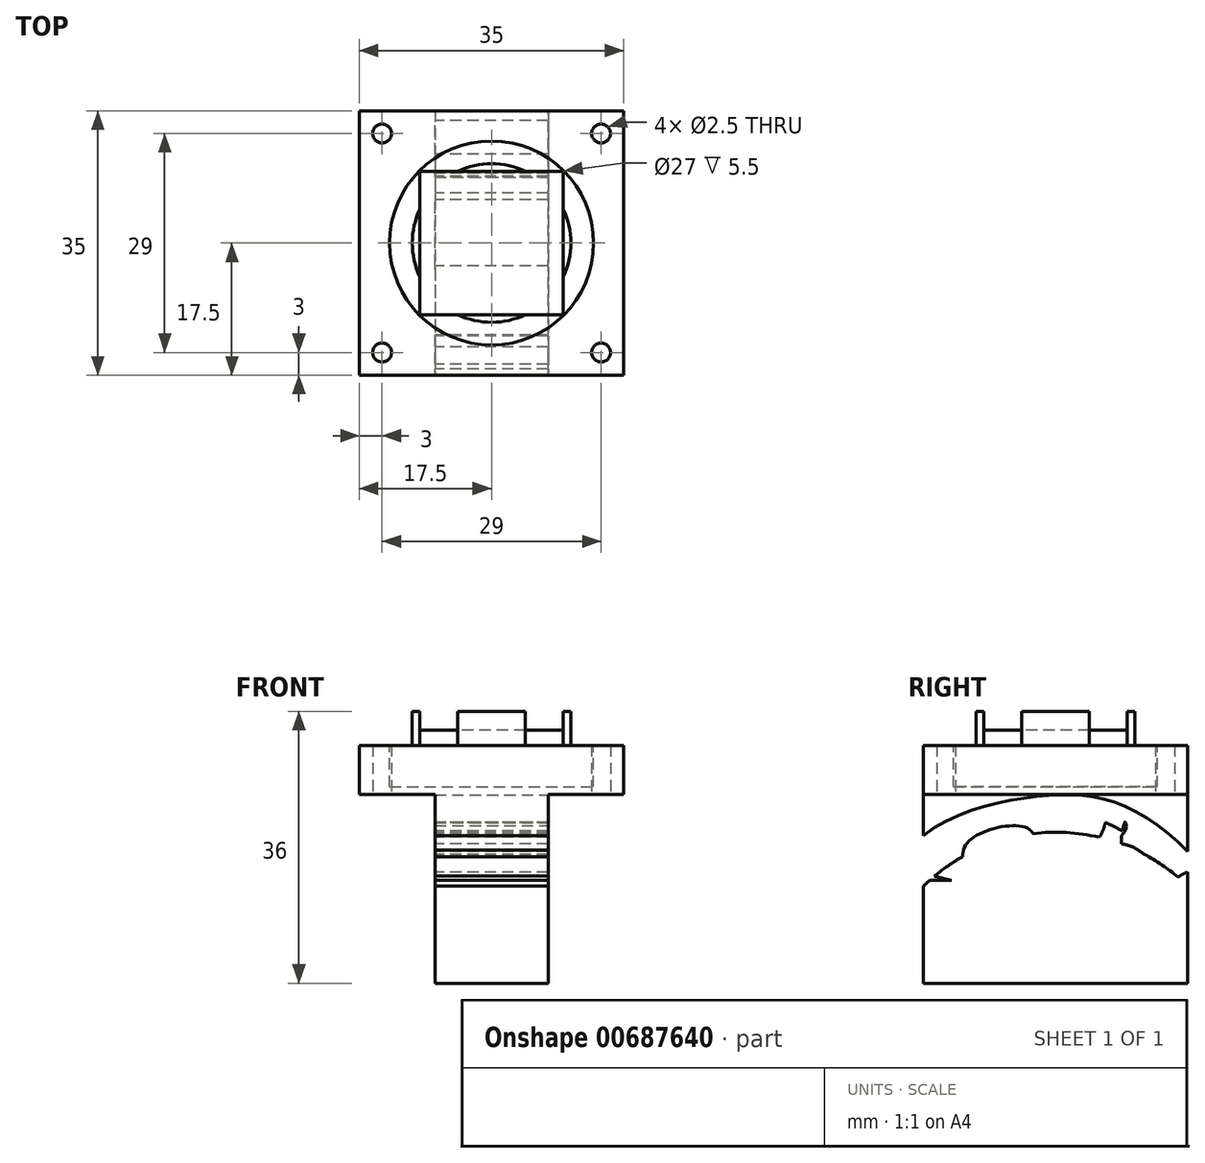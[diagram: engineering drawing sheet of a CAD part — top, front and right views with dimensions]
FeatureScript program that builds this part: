
annotation { "Feature Type Name" : "Feature", "Feature Type Description" : "" }
export const myFeature = defineFeature(function(context is Context, id is Id, definition is map)
    precondition{}
    {
        {
            var Q0;
            Q0=qCreatedBy(makeId("Top.planeOp"),FACE);
            var sketch = newSketch(context, id + "F0", { "sketchPlane" : qUnion([Q0])});
            skLineSegment(sketch, "E0", {"start": v(0, 0) * mm, "end": v(-19, 0) * mm});
            skLineSegment(sketch, "E1", {"start": v(-19, 0) * mm, "end": v(-19, 19) * mm});
            skLineSegment(sketch, "E2", {"start": v(-19, 19) * mm, "end": v(0, 19) * mm});
            skLineSegment(sketch, "E3", {"start": v(0, 19) * mm, "end": v(0, 0) * mm});
            skLineSegment(sketch, "E4.0", {"start": v(2, -2) * mm, "end": v(-21, -2) * mm});
            skLineSegment(sketch, "E4.1", {"start": v(2, 21) * mm, "end": v(2, -2) * mm});
            skLineSegment(sketch, "E4.2", {"start": v(-21, 21) * mm, "end": v(2, 21) * mm});
            skLineSegment(sketch, "E4.3", {"start": v(-21, -2) * mm, "end": v(-21, 21) * mm});
            skCircle(sketch, "E5", {"center": v(-9.5, 9.5) * mm, "radius": 10.5 * mm});
            skPoint(sketch, "E5.centerSnap0", {"position": v(-9.5, 0) * mm});
            skPoint(sketch, "E5.centerSnap1", {"position": v(0, 9.5) * mm});
            skLineSegment(sketch, "E6.0", {"start": v(8, -8) * mm, "end": v(-27, -8) * mm});
            skLineSegment(sketch, "E6.1", {"start": v(8, 27) * mm, "end": v(8, -8) * mm});
            skLineSegment(sketch, "E6.2", {"start": v(-27, 27) * mm, "end": v(8, 27) * mm});
            skLineSegment(sketch, "E6.3", {"start": v(-27, -8) * mm, "end": v(-27, 27) * mm});
            skLineSegment(sketch, "E7", {"start": v(-27, -8) * mm, "end": v(-21, -2) * mm});
            skLineSegment(sketch, "E8", {"start": v(-27, -8) * mm, "end": v(-24, -5) * mm});
            skLineSegment(sketch, "E9", {"start": v(-9.5, 9.5) * mm, "end": v(-11.5, 9.5) * mm});
            skLineSegment(sketch, "E10", {"start": v(-9.5, 9.5) * mm, "end": v(-9.5, 11.53) * mm});
            skLineSegment(sketch, "E11.MirrorCS", {"start": v(-27, 27) * mm, "end": v(-24, 24) * mm});
            skLineSegment(sketch, "E12.MirrorCS", {"start": v(8, -8) * mm, "end": v(5, -5) * mm});
            skLineSegment(sketch, "E13.MirrorCS", {"start": v(8, 27) * mm, "end": v(5, 24) * mm});
            skSolve(sketch);
        }
        {
            var Q0;
            Q0=qSketchRegion(id+"F0",true);
            var Q1;
            {var subQ0=sQuery(id+"F0.wireOp",EDGE,"E5");var subQ1=sQuery(id+"F0.wireOp",EDGE,"E3");var subQ2=makeQuery(id+"F0.imprint","INTERSECT",VERTEX,{"disambiguationData":[OD(0.0)],"derivedFrom":[subQ1,subQ0]});Q1=makeQuery(id+"F0.imprint","IMPRINT",FACE,{"disambiguationData":[TD([[makeQuery(id+"F0.imprint","IMPRINT",EDGE,{"disambiguationData":[TD([[subQ2,-1.0]])],"derivedFrom":subQ1}),1.0]])]});}
            var Q2;
            {var subQ0=sQuery(id+"F0.wireOp",EDGE,"E5");var subQ1=sQuery(id+"F0.wireOp",EDGE,"E0");var subQ2=makeQuery(id+"F0.imprint","INTERSECT",VERTEX,{"disambiguationData":[OD(0.0)],"derivedFrom":[subQ1,subQ0]});Q2=makeQuery(id+"F0.imprint","IMPRINT",FACE,{"disambiguationData":[TD([[makeQuery(id+"F0.imprint","IMPRINT",EDGE,{"disambiguationData":[TD([[subQ2,-1.0]])],"derivedFrom":subQ1}),1.0]])]});}
            var Q3;
            {var subQ0=sQuery(id+"F0.wireOp",EDGE,"E5");var subQ1=sQuery(id+"F0.wireOp",EDGE,"E1");var subQ2=makeQuery(id+"F0.imprint","INTERSECT",VERTEX,{"disambiguationData":[OD(0.0)],"derivedFrom":[subQ1,subQ0]});Q3=makeQuery(id+"F0.imprint","IMPRINT",FACE,{"disambiguationData":[TD([[makeQuery(id+"F0.imprint","IMPRINT",EDGE,{"disambiguationData":[TD([[subQ2,-1.0]])],"derivedFrom":subQ1}),1.0]])]});}
            var Q4;
            {var subQ0=sQuery(id+"F0.wireOp",EDGE,"E5");var subQ1=sQuery(id+"F0.wireOp",EDGE,"E2");var subQ2=makeQuery(id+"F0.imprint","INTERSECT",VERTEX,{"disambiguationData":[OD(0.0)],"derivedFrom":[subQ1,subQ0]});Q4=makeQuery(id+"F0.imprint","IMPRINT",FACE,{"disambiguationData":[TD([[makeQuery(id+"F0.imprint","IMPRINT",EDGE,{"disambiguationData":[TD([[subQ2,-1.0]])],"derivedFrom":subQ1}),1.0]])]});}
            var Q5;
            {var subQ0=sQuery(id+"F0.wireOp",EDGE,"E2");var subQ1=sQuery(id+"F0.wireOp",EDGE,"E1");var subQ2=makeQuery(id+"F0.imprint","INTERSECT",VERTEX,{"derivedFrom":[subQ1,subQ0]});Q5=makeQuery(id+"F0.imprint","IMPRINT",FACE,{"disambiguationData":[TD([[makeQuery(id+"F0.imprint","IMPRINT",EDGE,{"disambiguationData":[TD([[subQ2,1.0]])],"derivedFrom":subQ1}),-1.0]])]});}
            var Q6;
            {var subQ0=sQuery(id+"F0.wireOp",EDGE,"E3");var subQ1=sQuery(id+"F0.wireOp",EDGE,"E2");var subQ2=makeQuery(id+"F0.imprint","INTERSECT",VERTEX,{"derivedFrom":[subQ1,subQ0]});Q6=makeQuery(id+"F0.imprint","IMPRINT",FACE,{"disambiguationData":[TD([[makeQuery(id+"F0.imprint","IMPRINT",EDGE,{"disambiguationData":[TD([[subQ2,1.0]])],"derivedFrom":subQ1}),-1.0]])]});}
            var Q7;
            {var subQ0=sQuery(id+"F0.wireOp",EDGE,"E3");var subQ1=sQuery(id+"F0.wireOp",EDGE,"E0");var subQ2=makeQuery(id+"F0.imprint","INTERSECT",VERTEX,{"derivedFrom":[subQ1,subQ0]});Q7=makeQuery(id+"F0.imprint","IMPRINT",FACE,{"disambiguationData":[TD([[makeQuery(id+"F0.imprint","IMPRINT",EDGE,{"disambiguationData":[TD([[subQ2,-1.0]])],"derivedFrom":subQ1}),-1.0]])]});}
            var Q8;
            {var subQ0=sQuery(id+"F0.wireOp",EDGE,"E1");var subQ1=sQuery(id+"F0.wireOp",EDGE,"E0");var subQ2=makeQuery(id+"F0.imprint","INTERSECT",VERTEX,{"derivedFrom":[subQ1,subQ0]});Q8=makeQuery(id+"F0.imprint","IMPRINT",FACE,{"disambiguationData":[TD([[makeQuery(id+"F0.imprint","IMPRINT",EDGE,{"disambiguationData":[TD([[subQ2,1.0]])],"derivedFrom":subQ1}),-1.0]])]});}
            var Q9;
            Q9=makeQuery(id+"F0.imprint","IMPRINT",FACE,{"disambiguationData":[TD([[makeQuery(id+"F0.imprint","IMPRINT",EDGE,{"derivedFrom":sQuery(id+"F0.wireOp",EDGE,"E4.0")}),-1.0]])]});
            var Q10;
            {var subQ0=sQuery(id+"F0.wireOp",EDGE,"E5");var subQ10=sQuery(id+"F0.wireOp",EDGE,"E0");var subQ11=makeQuery(id+"F0.imprint","INTERSECT",VERTEX,{"disambiguationData":[OD(0.0)],"derivedFrom":[subQ10,subQ0]});Q10=makeQuery(id+"F0.imprint","IMPRINT",FACE,{"disambiguationData":[TD([[makeQuery(id+"F0.imprint","IMPRINT",EDGE,{"disambiguationData":[TD([[subQ11,-1.0]])],"derivedFrom":subQ10}),-1.0]])]});}
            extrude(context, id + "F1", {"entities" : qUnion([Q0, Q1, Q2, Q3, Q4, Q5, Q6, Q7, Q8, Q9, Q10]), "oppositeDirection" : true, "depth" : 2 * mm, "offsetDistance" : 25 * mm});
        }
        {
            var Q0;
            Q0=makeQuery(id+"F1.opExtrude","CAP_FACE",FACE,{"disambiguationData":[OSD([sQuery(id+"F0.wireOp",EDGE,"E6.0"),sQuery(id+"F0.wireOp",EDGE,"E6.1"),sQuery(id+"F0.wireOp",EDGE,"E6.2"),sQuery(id+"F0.wireOp",EDGE,"E6.3")])],"isStart":false});
            var sketch = newSketch(context, id + "F2", { "sketchPlane" : qUnion([Q0])});
            skLineSegment(sketch, "E14", {"start": v(-27, -27) * mm, "end": v(-27, 8) * mm});
            skLineSegment(sketch, "E15", {"start": v(-27, 8) * mm, "end": v(8, 8) * mm});
            skLineSegment(sketch, "E16", {"start": v(8, 8) * mm, "end": v(8, -27) * mm});
            skLineSegment(sketch, "E17", {"start": v(8, -27) * mm, "end": v(-27, -27) * mm});
            skLineSegment(sketch, "E18", {"start": v(-27, -9.5) * mm, "end": v(8, -9.5) * mm});
            skCircle(sketch, "E19", {"center": v(-9.5, -9.5) * mm, "radius": 13.5 * mm});
            skSolve(sketch);
        }
        {
            var Q0;
            Q0=qSketchRegion(id+"F2",true);
            extrude(context, id + "F3", {"entities" : qUnion([Q0]), "depth" : 5.5 * mm, "offsetDistance" : 25 * mm});
        }
        {
            var Q0;
            {var subQ0=sQuery(id+"F0.wireOp",EDGE,"E5");var subQ1=sQuery(id+"F0.wireOp",EDGE,"E1");var subQ2=makeQuery(id+"F0.imprint","INTERSECT",VERTEX,{"disambiguationData":[OD(0.0)],"derivedFrom":[subQ1,subQ0]});Q0=makeQuery(id+"F0.imprint","IMPRINT",FACE,{"disambiguationData":[TD([[makeQuery(id+"F0.imprint","IMPRINT",EDGE,{"disambiguationData":[TD([[subQ2,-1.0]])],"derivedFrom":subQ1}),1.0]])]});}
            var Q1;
            {var subQ0=sQuery(id+"F0.wireOp",EDGE,"E5");var subQ1=sQuery(id+"F0.wireOp",EDGE,"E2");var subQ2=makeQuery(id+"F0.imprint","INTERSECT",VERTEX,{"disambiguationData":[OD(0.0)],"derivedFrom":[subQ1,subQ0]});Q1=makeQuery(id+"F0.imprint","IMPRINT",FACE,{"disambiguationData":[TD([[makeQuery(id+"F0.imprint","IMPRINT",EDGE,{"disambiguationData":[TD([[subQ2,-1.0]])],"derivedFrom":subQ1}),1.0]])]});}
            var Q2;
            {var subQ0=sQuery(id+"F0.wireOp",EDGE,"E5");var subQ1=sQuery(id+"F0.wireOp",EDGE,"E3");var subQ2=makeQuery(id+"F0.imprint","INTERSECT",VERTEX,{"disambiguationData":[OD(0.0)],"derivedFrom":[subQ1,subQ0]});Q2=makeQuery(id+"F0.imprint","IMPRINT",FACE,{"disambiguationData":[TD([[makeQuery(id+"F0.imprint","IMPRINT",EDGE,{"disambiguationData":[TD([[subQ2,-1.0]])],"derivedFrom":subQ1}),1.0]])]});}
            var Q3;
            {var subQ0=sQuery(id+"F0.wireOp",EDGE,"E5");var subQ1=sQuery(id+"F0.wireOp",EDGE,"E0");var subQ2=makeQuery(id+"F0.imprint","INTERSECT",VERTEX,{"disambiguationData":[OD(0.0)],"derivedFrom":[subQ1,subQ0]});Q3=makeQuery(id+"F0.imprint","IMPRINT",FACE,{"disambiguationData":[TD([[makeQuery(id+"F0.imprint","IMPRINT",EDGE,{"disambiguationData":[TD([[subQ2,-1.0]])],"derivedFrom":subQ1}),1.0]])]});}
            var Q4;
            Q4=makeQuery(id+"F0.imprint","IMPRINT",FACE,{"disambiguationData":[TD([[makeQuery(id+"F0.imprint","IMPRINT",EDGE,{"derivedFrom":sQuery(id+"F0.wireOp",EDGE,"E4.0")}),-1.0]])]});
            extrude(context, id + "F4", {"entities" : qUnion([Q0, Q1, Q2, Q3, Q4]), "operationType" : NewBodyOperationType.ADD, "depth" : 2.5 * mm, "offsetDistance" : 25 * mm});
        }
        {
            var Q0;
            Q0=makeQuery(id+"F3.opExtrude","CAP_FACE",FACE,{"disambiguationData":[OSD([sQuery(id+"F2.wireOp",EDGE,"E14"),sQuery(id+"F2.wireOp",EDGE,"E15"),sQuery(id+"F2.wireOp",EDGE,"E16"),sQuery(id+"F2.wireOp",EDGE,"E17"),sQuery(id+"F2.wireOp",EDGE,"E19")])],"isStart":false});
            var Q1;
            Q1=makeQuery(id+"F1.opExtrude","CAP_FACE",FACE,{"disambiguationData":[OSD([sQuery(id+"F0.wireOp",EDGE,"E6.0"),sQuery(id+"F0.wireOp",EDGE,"E6.1"),sQuery(id+"F0.wireOp",EDGE,"E6.2"),sQuery(id+"F0.wireOp",EDGE,"E6.3")])],"isStart":false});
            extrude(context, id + "F5", {"entities" : qUnion([Q0, Q1]), "depth" : 1 * mm, "offsetDistance" : 25 * mm});
        }
        {
            var Q0;
            Q0=makeQuery(id+"F5.opExtrude","SWEPT_BODY",BODY,{"disambiguationData":[OSD([sQuery(id+"F2.wireOp",EDGE,"E14"),sQuery(id+"F2.wireOp",EDGE,"E15"),sQuery(id+"F2.wireOp",EDGE,"E16"),sQuery(id+"F2.wireOp",EDGE,"E17"),sQuery(id+"F2.wireOp",EDGE,"E19")])]});
            var Q1;
            Q1=makeQuery(id+"F5.opExtrude","SWEPT_BODY",BODY,{"disambiguationData":[OSD([sQuery(id+"F0.wireOp",EDGE,"E6.0"),sQuery(id+"F0.wireOp",EDGE,"E6.1"),sQuery(id+"F0.wireOp",EDGE,"E6.2"),sQuery(id+"F0.wireOp",EDGE,"E6.3")])]});
            deleteBodies(context, id + "F6", {"entities" : qUnion([Q0, Q1])});
        }
        {
            var Q0;
            Q0=makeQuery(id+"F3.opExtrude","CAP_FACE",FACE,{"disambiguationData":[OSD([sQuery(id+"F2.wireOp",EDGE,"E14"),sQuery(id+"F2.wireOp",EDGE,"E15"),sQuery(id+"F2.wireOp",EDGE,"E16"),sQuery(id+"F2.wireOp",EDGE,"E17"),sQuery(id+"F2.wireOp",EDGE,"E19")])],"isStart":false});
            var sketch = newSketch(context, id + "F7", { "sketchPlane" : qUnion([Q0])});
            skLineSegment(sketch, "E20", {"start": v(-27, -27) * mm, "end": v(8, -27) * mm});
            skLineSegment(sketch, "E21", {"start": v(8, -27) * mm, "end": v(8, 8) * mm});
            skLineSegment(sketch, "E22", {"start": v(8, 8) * mm, "end": v(-27, 8) * mm});
            skLineSegment(sketch, "E23", {"start": v(-27, 8) * mm, "end": v(-27, -27) * mm});
            skSolve(sketch);
        }
        {
            var Q0;
            Q0=makeQuery(id+"F7.imprint","IMPRINT",FACE,{"disambiguationData":[TD([[makeQuery(id+"F7.imprint","IMPRINT",EDGE,{"derivedFrom":sQuery(id+"F7.wireOp",EDGE,"E20")}),1.0]])]});
            var Q1;
            Q1=makeQuery(id+"F7.imprint","IMPRINT",FACE,{"disambiguationData":[TD([[makeQuery(id+"F7.imprint","IMPRINT",EDGE,{"derivedFrom":makeQuery(id+"FP3SZp29wrBzVes_1.hole-0.boolean.opBoolean","INTERSECT",EDGE,{"derivedFrom":[makeQuery(id+"F3.opExtrude","CAP_FACE",FACE,{"disambiguationData":[OSD([sQuery(id+"F2.wireOp",EDGE,"E14"),sQuery(id+"F2.wireOp",EDGE,"E15"),sQuery(id+"F2.wireOp",EDGE,"E16"),sQuery(id+"F2.wireOp",EDGE,"E17"),sQuery(id+"F2.wireOp",EDGE,"E19")])],"isStart":false}),makeQuery(id+"FP3SZp29wrBzVes_1.hole-0.opRevolve","SWEPT_FACE",FACE,{"disambiguationData":[OSD([sQuery(id+"FP3SZp29wrBzVes_1.hole-0.sketch.wireOp",EDGE,"core_line_2")])]})]})}),-1.0]])]});
            var Q2;
            Q2=makeQuery(id+"F7.imprint","IMPRINT",FACE,{"disambiguationData":[TD([[makeQuery(id+"F7.imprint","IMPRINT",EDGE,{"derivedFrom":makeQuery(id+"FP3SZp29wrBzVes_1.hole-1.boolean.opBoolean","INTERSECT",EDGE,{"derivedFrom":[makeQuery(id+"F3.opExtrude","CAP_FACE",FACE,{"disambiguationData":[OSD([sQuery(id+"F2.wireOp",EDGE,"E14"),sQuery(id+"F2.wireOp",EDGE,"E15"),sQuery(id+"F2.wireOp",EDGE,"E16"),sQuery(id+"F2.wireOp",EDGE,"E17"),sQuery(id+"F2.wireOp",EDGE,"E19")])],"isStart":false}),makeQuery(id+"FP3SZp29wrBzVes_1.hole-1.opRevolve","SWEPT_FACE",FACE,{"disambiguationData":[OSD([sQuery(id+"FP3SZp29wrBzVes_1.hole-1.sketch.wireOp",EDGE,"core_line_2")])]})]})}),-1.0]])]});
            var Q3;
            Q3=makeQuery(id+"F7.imprint","IMPRINT",FACE,{"disambiguationData":[TD([[makeQuery(id+"F7.imprint","IMPRINT",EDGE,{"derivedFrom":makeQuery(id+"FP3SZp29wrBzVes_1.hole-3.boolean.opBoolean","INTERSECT",EDGE,{"derivedFrom":[makeQuery(id+"F3.opExtrude","CAP_FACE",FACE,{"disambiguationData":[OSD([sQuery(id+"F2.wireOp",EDGE,"E14"),sQuery(id+"F2.wireOp",EDGE,"E15"),sQuery(id+"F2.wireOp",EDGE,"E16"),sQuery(id+"F2.wireOp",EDGE,"E17"),sQuery(id+"F2.wireOp",EDGE,"E19")])],"isStart":false}),makeQuery(id+"FP3SZp29wrBzVes_1.hole-3.opRevolve","SWEPT_FACE",FACE,{"disambiguationData":[OSD([sQuery(id+"FP3SZp29wrBzVes_1.hole-3.sketch.wireOp",EDGE,"core_line_2")])]})]})}),-1.0]])]});
            var Q4;
            Q4=makeQuery(id+"F7.imprint","IMPRINT",FACE,{"disambiguationData":[TD([[makeQuery(id+"F7.imprint","IMPRINT",EDGE,{"derivedFrom":makeQuery(id+"F3.opExtrude","CAP_EDGE",EDGE,{"disambiguationData":[OSD([sQuery(id+"F2.wireOp",EDGE,"E19")])],"isStart":false})}),1.0]])]});
            var Q5;
            Q5=makeQuery(id+"F7.imprint","IMPRINT",FACE,{"disambiguationData":[TD([[makeQuery(id+"F7.imprint","IMPRINT",EDGE,{"derivedFrom":makeQuery(id+"FP3SZp29wrBzVes_1.hole-2.boolean.opBoolean","INTERSECT",EDGE,{"derivedFrom":[makeQuery(id+"F3.opExtrude","CAP_FACE",FACE,{"disambiguationData":[OSD([sQuery(id+"F2.wireOp",EDGE,"E14"),sQuery(id+"F2.wireOp",EDGE,"E15"),sQuery(id+"F2.wireOp",EDGE,"E16"),sQuery(id+"F2.wireOp",EDGE,"E17"),sQuery(id+"F2.wireOp",EDGE,"E19")])],"isStart":false}),makeQuery(id+"FP3SZp29wrBzVes_1.hole-2.opRevolve","SWEPT_FACE",FACE,{"disambiguationData":[OSD([sQuery(id+"FP3SZp29wrBzVes_1.hole-2.sketch.wireOp",EDGE,"core_line_2")])]})]})}),-1.0]])]});
            extrude(context, id + "F8", {"entities" : qUnion([Q0, Q1, Q2, Q3, Q4, Q5]), "operationType" : NewBodyOperationType.ADD, "depth" : 1 * mm, "offsetDistance" : 25 * mm});
        }
        {
            var Q0;
            Q0=sQuery(id+"F0.wireOp",VERTEX,"E8.end");
            var Q1;
            Q1=sQuery(id+"F0.wireOp",VERTEX,"E11.MirrorCS.end");
            var Q2;
            Q2=sQuery(id+"F0.wireOp",VERTEX,"E13.MirrorCS.end");
            var Q3;
            Q3=sQuery(id+"F0.wireOp",VERTEX,"E12.MirrorCS.end");
            var Q4;
            Q4=makeQuery(id+"F3.opExtrude","SWEPT_BODY",BODY,{"disambiguationData":[OSD([sQuery(id+"F2.wireOp",EDGE,"E14"),sQuery(id+"F2.wireOp",EDGE,"E15"),sQuery(id+"F2.wireOp",EDGE,"E16"),sQuery(id+"F2.wireOp",EDGE,"E17"),sQuery(id+"F2.wireOp",EDGE,"E19")])]});
            var Q5;
            Q5=makeQuery(id+"F1.opExtrude","SWEPT_BODY",BODY,{"disambiguationData":[OSD([sQuery(id+"F0.wireOp",EDGE,"E6.0"),sQuery(id+"F0.wireOp",EDGE,"E6.1"),sQuery(id+"F0.wireOp",EDGE,"E6.2"),sQuery(id+"F0.wireOp",EDGE,"E6.3")])]});
            hole(context, id + "F9", {"style" : HoleStyle.SIMPLE, "endStyle" : HoleEndStyle.BLIND, "holeDiameter" : 2.5 * mm, "majorDiameter" : 5 * mm, "holeDepth" : 10 * mm, "isTappedThrough" : true, "tappedDepth" : 12 * mm, "tapClearance" : 3, "locations" : qUnion([Q0, Q1, Q2, Q3]), "scope" : qUnion([Q4, Q5]), "startStyle" : HoleStartStyle.PART});
        }
        {
            var Q0;
            Q0=makeQuery(id+"F8.opExtrude","CAP_FACE",FACE,{"disambiguationData":[OSD([sQuery(id+"F7.wireOp",EDGE,"E20"),sQuery(id+"F7.wireOp",EDGE,"E21"),sQuery(id+"F7.wireOp",EDGE,"E22"),sQuery(id+"F7.wireOp",EDGE,"E23")])],"isStart":false});
            var sketch = newSketch(context, id + "F10", { "sketchPlane" : qUnion([Q0])});
            skLineSegment(sketch, "E24", {"start": v(-27, 8) * mm, "end": v(8, 8) * mm});
            skLineSegment(sketch, "E25", {"start": v(8, 8) * mm, "end": v(8, -27) * mm});
            skLineSegment(sketch, "E26", {"start": v(8, -27) * mm, "end": v(-27, -27) * mm});
            skLineSegment(sketch, "E27", {"start": v(-27, -27) * mm, "end": v(-27, 8) * mm});
            skLineSegment(sketch, "E28", {"start": v(-9.5, 8) * mm, "end": v(-9.5, -27) * mm});
            skLineSegment(sketch, "E29", {"start": v(-9.5, -9.5) * mm, "end": v(-17, -9.5) * mm});
            skLineSegment(sketch, "E30", {"start": v(-17, -9.5) * mm, "end": v(-17, 8) * mm});
            skLineSegment(sketch, "E31.MirrorCS", {"start": v(-2, -9.5) * mm, "end": v(-2, 8) * mm});
            skLineSegment(sketch, "E32.MirrorCS", {"start": v(-17, -9.5) * mm, "end": v(-17, -27) * mm});
            skLineSegment(sketch, "E33.MirrorCS", {"start": v(-2, -9.5) * mm, "end": v(-2, -27) * mm});
            skSolve(sketch);
        }
        {
            var Q0;
            {var subQ4=sQuery(id+"F10.wireOp",EDGE,"E29");Q0=makeQuery(id+"F10.imprint","IMPRINT",FACE,{"disambiguationData":[TD([[makeQuery(id+"F10.imprint","IMPRINT",EDGE,{"derivedFrom":subQ4}),-1.0]])]});}
            var Q1;
            {var subQ4=sQuery(id+"F10.wireOp",EDGE,"E29");Q1=makeQuery(id+"F10.imprint","IMPRINT",FACE,{"disambiguationData":[TD([[makeQuery(id+"F10.imprint","IMPRINT",EDGE,{"derivedFrom":subQ4}),1.0]])]});}
            var Q2;
            {var subQ7=sQuery(id+"F10.wireOp",EDGE,"E31.MirrorCS");Q2=makeQuery(id+"F10.imprint","IMPRINT",FACE,{"disambiguationData":[TD([[makeQuery(id+"F10.imprint","IMPRINT",EDGE,{"derivedFrom":subQ7}),1.0]])]});}
            extrude(context, id + "F11", {"entities" : qUnion([Q0, Q1, Q2]), "operationType" : NewBodyOperationType.ADD, "depth" : 25 * mm, "offsetDistance" : 25 * mm});
        }
        {
            var Q0;
            Q0=makeQuery(id+"F11.opExtrude","SWEPT_FACE",FACE,{"disambiguationData":[OSD([sQuery(id+"F10.wireOp",EDGE,"E30"),sQuery(id+"F10.wireOp",EDGE,"E32.MirrorCS")])]});
            var sketch = newSketch(context, id + "F12", { "sketchPlane" : qUnion([Q0])});
            skLineSegment(sketch, "E34", {"start": v(-9.5, -33.5) * mm, "end": v(-9.5, -38.5) * mm});
            skCircle(sketch, "E35", {"center": v(-9.5, -38.5) * mm, "radius": 25 * mm});
            skLineSegment(sketch, "E36", {"start": v(-34.27, -35.15) * mm, "end": v(-34.82, -35.15) * mm});
            skLineSegment(sketch, "E37", {"start": v(15.27, -35.15) * mm, "end": v(16.76, -35.15) * mm});
            skFitSpline(sketch, "E38.trimOffspring", {"points": [v(-30.82, -35.15) * mm, v(-30.8, -34.42) * mm, v(-30.07, -31.8) * mm, v(-28.76, -30.16) * mm, v(-28.76, -29.96) * mm, v(-31.33, -28.27) * mm, v(-29.32, -24.95) * mm, v(-25.57, -27.52) * mm, v(-24.17, -24.67) * mm, v(-27.91, -21.16) * mm, v(-27.21, -18.81) * mm, v(-23.89, -20.6) * mm, v(-23.13, -18.79) * mm, v(-19.12, -15.24) * mm, v(-17.54, -14.77) * mm, v(-18.88, -12.72) * mm, v(-16.76, -11.23) * mm, v(-15.18, -14.22) * mm, v(-12.35, -13.43) * mm, v(-12.19, -10.83) * mm, v(-9.9, -10.2) * mm, v(-9.15, -13.2) * mm, v(-9.15, -14.7) * mm, v(-7.27, -15.44) * mm, v(-6.01, -13.12) * mm, v(2.3, -15.04) * mm, v(2.73, -19.15) * mm, v(4.28, -19.88) * mm, v(9.02, -19.51) * mm, v(12.33, -28.71) * mm, v(11.67, -31.4) * mm, v(12.36, -33.05) * mm, v(12.76, -35.15) * mm], "startDerivative": vector(-4.1, 38.5) * mm, "endDerivative": vector(7.13, -81.47) * mm});
            skFitSpline(sketch, "E39", {"points": [v(-34.82, -35.15) * mm, v(-31.65, -22.25) * mm, v(-19.5, -10.45) * mm, v(-7.04, -8.78) * mm, v(9.33, -15.12) * mm, v(16.76, -35.15) * mm], "startDerivative": vector(7.36, 71.63) * mm, "endDerivative": vector(18.66, -100.82) * mm});
            skFitSpline(sketch, "E40", {"points": [v(-23.89, -20.6) * mm, v(-21.86, -17.7) * mm, v(-19.61, -15.93) * mm, v(-19.12, -15.24) * mm], "startDerivative": vector(4.2, 7.4) * mm, "endDerivative": vector(1.7, 3.17) * mm});
            skFitSpline(sketch, "E41", {"points": [v(-19.61, -15.93) * mm, v(-18.25, -15.05) * mm, v(-18.7, -12.15) * mm, v(-18.72, -12.18) * mm], "startDerivative": vector(4.52, 0.75) * mm, "endDerivative": vector(-0.25, -1.01) * mm});
            skFitSpline(sketch, "E42", {"points": [v(-18.34, -13.33) * mm, v(-16.1, -12.25) * mm, v(-16.1, -12.26) * mm], "startDerivative": vector(3.49, 1.78) * mm, "endDerivative": vector(-0.02, -0.22) * mm});
            skFitSpline(sketch, "E43", {"points": [v(-12.3, -11.5) * mm, v(-9.15, -11.69) * mm], "startDerivative": vector(3.16, -0.18) * mm, "endDerivative": vector(3.16, -0.18) * mm});
            skFitSpline(sketch, "E44", {"points": [v(-6.01, -13.12) * mm, v(-1.19, -14.22) * mm, v(2.7, -15.88) * mm], "startDerivative": vector(9.6, -1.77) * mm, "endDerivative": vector(7.8, -3.77) * mm});
            skFitSpline(sketch, "E45", {"points": [v(4.28, -19.88) * mm, v(12.61, -19.88) * mm], "startDerivative": vector(8.33, 0) * mm, "endDerivative": vector(8.33, 0) * mm});
            skFitSpline(sketch, "E46", {"points": [v(-27.21, -18.81) * mm, v(-29.4, -18.81) * mm], "startDerivative": vector(-2.19, 0) * mm, "endDerivative": vector(-2.19, 0) * mm});
            skLineSegment(sketch, "E47", {"start": v(-2.76, -13.78) * mm, "end": v(-2.76, -19.07) * mm});
            skLineSegment(sketch, "E48", {"start": v(-2.76, -19.07) * mm, "end": v(-1.19, -19.07) * mm});
            skLineSegment(sketch, "E49", {"start": v(-1.19, -19.07) * mm, "end": v(-1.19, -14.22) * mm});
            skLineSegment(sketch, "E50", {"start": v(-1.19, -19.07) * mm, "end": v(0.46, -14.84) * mm});
            skSolve(sketch);
        }
        {
            var Q0;
            Q0=makeQuery(id+"F1.opExtrude","SWEPT_BODY",BODY,{"disambiguationData":[OSD([sQuery(id+"F0.wireOp",EDGE,"E6.0"),sQuery(id+"F0.wireOp",EDGE,"E6.1"),sQuery(id+"F0.wireOp",EDGE,"E6.2"),sQuery(id+"F0.wireOp",EDGE,"E6.3")])]});
            deleteBodies(context, id + "F13", {"entities" : qUnion([Q0])});
        }
        {
            var Q0;
            {var subQ0=sQuery(id+"F12.wireOp",EDGE,"E45");var subQ1=sQuery(id+"F12.wireOp",EDGE,"E35");var subQ2=makeQuery(id+"F12.imprint","INTERSECT",VERTEX,{"derivedFrom":[subQ1,subQ0]});Q0=makeQuery(id+"F12.imprint","IMPRINT",FACE,{"disambiguationData":[TD([[makeQuery(id+"F12.imprint","IMPRINT",EDGE,{"disambiguationData":[TD([[subQ2,-1.0]])],"derivedFrom":subQ1}),-1.0]])]});}
            var Q1;
            {var subQ0=sQuery(id+"F12.wireOp",EDGE,"E45");var subQ1=sQuery(id+"F12.wireOp",EDGE,"E35");var subQ2=makeQuery(id+"F12.imprint","INTERSECT",VERTEX,{"derivedFrom":[subQ1,subQ0]});Q1=makeQuery(id+"F12.imprint","IMPRINT",FACE,{"disambiguationData":[TD([[makeQuery(id+"F12.imprint","IMPRINT",EDGE,{"disambiguationData":[TD([[subQ2,-1.0]])],"derivedFrom":subQ1}),1.0]])]});}
            var Q2;
            {var subQ22=sQuery(id+"F12.wireOp",EDGE,"E48");Q2=makeQuery(id+"F12.imprint","IMPRINT",FACE,{"disambiguationData":[TD([[makeQuery(id+"F12.imprint","IMPRINT",EDGE,{"derivedFrom":subQ22}),-1.0]])]});}
            var Q3;
            {var subQ4=sQuery(id+"F12.wireOp",EDGE,"E43");Q3=makeQuery(id+"F12.imprint","IMPRINT",FACE,{"disambiguationData":[TD([[makeQuery(id+"F12.imprint","IMPRINT",EDGE,{"derivedFrom":subQ4}),-1.0]])]});}
            var Q4;
            {var subQ0=sQuery(id+"F12.wireOp",EDGE,"E43");Q4=makeQuery(id+"F12.imprint","IMPRINT",FACE,{"disambiguationData":[TD([[makeQuery(id+"F12.imprint","IMPRINT",EDGE,{"derivedFrom":subQ0}),1.0]])]});}
            var Q5;
            {var subQ1=sQuery(id+"F12.wireOp",EDGE,"E38.trimOffspring");var subQ3=sQuery(id+"F12.wireOp",EDGE,"E35");var subQ4=makeQuery(id+"F12.imprint","INTERSECT",VERTEX,{"disambiguationData":[OD(5.0)],"derivedFrom":[subQ3,subQ1]});Q5=makeQuery(id+"F12.imprint","IMPRINT",FACE,{"disambiguationData":[TD([[makeQuery(id+"F12.imprint","IMPRINT",EDGE,{"disambiguationData":[TD([[subQ4,-1.0]])],"derivedFrom":subQ3}),-1.0]])]});}
            var Q6;
            {var subQ0=sQuery(id+"F12.wireOp",EDGE,"E42");var subQ1=sQuery(id+"F12.wireOp",EDGE,"E41");var subQ2=makeQuery(id+"F12.imprint","INTERSECT",VERTEX,{"derivedFrom":[subQ1,subQ0]});Q6=makeQuery(id+"F12.imprint","IMPRINT",FACE,{"disambiguationData":[TD([[makeQuery(id+"F12.imprint","IMPRINT",EDGE,{"disambiguationData":[TD([[subQ2,-1.0]])],"derivedFrom":subQ1}),-1.0]])]});}
            var Q7;
            {var subQ0=sQuery(id+"F12.wireOp",EDGE,"E38.trimOffspring");var subQ1=sQuery(id+"F12.wireOp",EDGE,"E35");var subQ2=makeQuery(id+"F12.imprint","INTERSECT",VERTEX,{"derivedFrom":[subQ1,subQ0]});Q7=makeQuery(id+"F12.imprint","IMPRINT",FACE,{"disambiguationData":[TD([[makeQuery(id+"F12.imprint","IMPRINT",EDGE,{"disambiguationData":[TD([[subQ2,-1.0]])],"derivedFrom":subQ1}),-1.0]])]});}
            var Q8;
            {var subQ0=sQuery(id+"F12.wireOp",EDGE,"E45");var subQ1=sQuery(id+"F12.wireOp",EDGE,"E35");var subQ2=makeQuery(id+"F12.imprint","INTERSECT",VERTEX,{"derivedFrom":[subQ1,subQ0]});Q8=makeQuery(id+"F12.imprint","IMPRINT",FACE,{"disambiguationData":[TD([[makeQuery(id+"F12.imprint","IMPRINT",EDGE,{"disambiguationData":[TD([[subQ2,1.0]])],"derivedFrom":subQ1}),-1.0]])]});}
            extrude(context, id + "F14", {"entities" : qUnion([Q0, Q1, Q2, Q3, Q4, Q5, Q6, Q7, Q8]), "operationType" : NewBodyOperationType.REMOVE, "oppositeDirection" : true, "depth" : 25 * mm, "offsetDistance" : 25 * mm});
        }
    });
